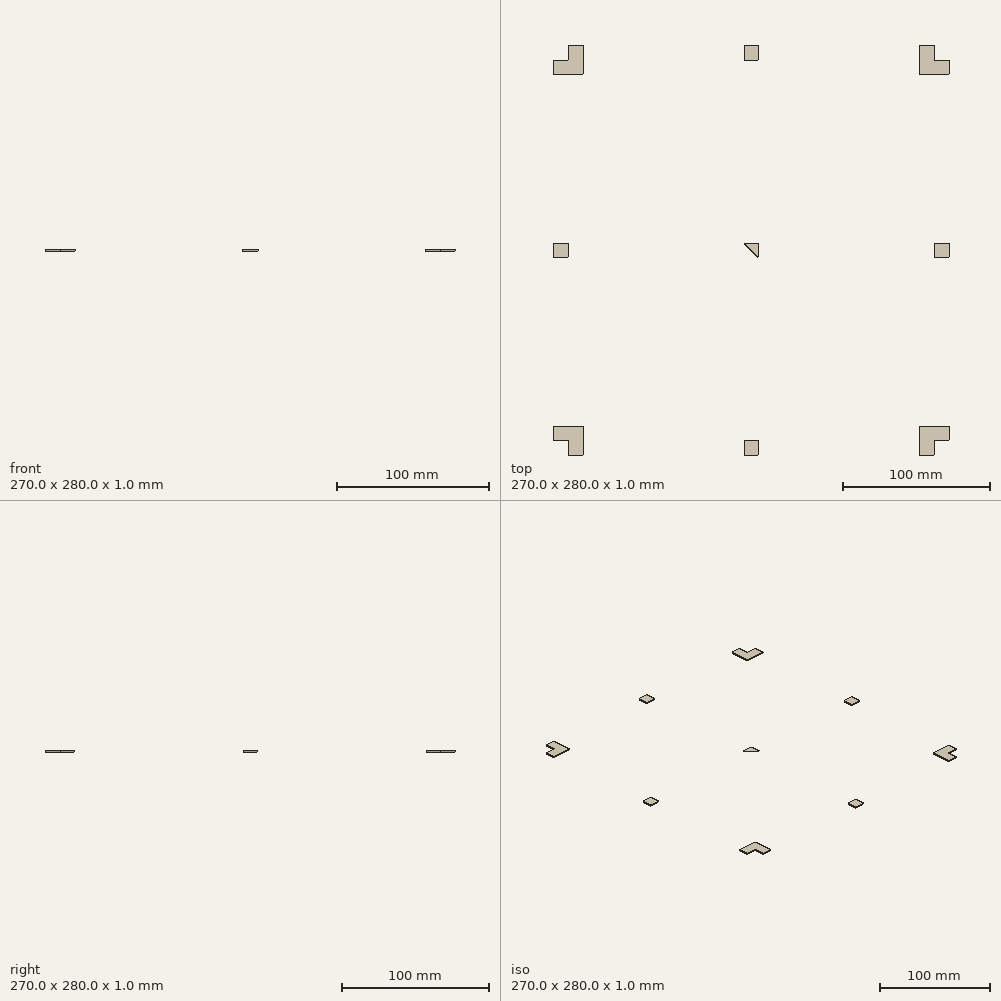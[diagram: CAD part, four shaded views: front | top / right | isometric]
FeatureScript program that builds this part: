
annotation { "Feature Type Name" : "Feature", "Feature Type Description" : "" }
export const myFeature = defineFeature(function(context is Context, id is Id, definition is map)
    precondition{}
    {
        {
            var Q0;
            Q0=qCreatedBy(makeId("Top.planeOp"),FACE);
            var sketch = newSketch(context, id + "F0", { "sketchPlane" : qUnion([Q0])});
            skLineSegment(sketch, "E0.bottom", {"start": v(-135, 140) * mm, "end": v(-115, 140) * mm});
            skLineSegment(sketch, "E0.top", {"start": v(-135, 120) * mm, "end": v(-115, 120) * mm});
            skLineSegment(sketch, "E0.left", {"start": v(-135, 140) * mm, "end": v(-135, 120) * mm});
            skLineSegment(sketch, "E0.right", {"start": v(-115, 140) * mm, "end": v(-115, 120) * mm});
            skSolve(sketch);
        }
        {
            var Q0;
            Q0 = qSketchRegion(id + "F0", true);
            extrude(context, id + "F1", {"entities" : qUnion([Q0]), "oppositeDirection" : true, "depth" : 1 * mm});
        }
        {
            var Q0;
            Q0=makeQuery(id+"F1.opExtrude","CAP_FACE",FACE,{"disambiguationData":[OSD([sQuery(id+"F0.wireOp",EDGE,"E0.bottom"),sQuery(id+"F0.wireOp",EDGE,"E0.top"),sQuery(id+"F0.wireOp",EDGE,"E0.left"),sQuery(id+"F0.wireOp",EDGE,"E0.right")])],"isStart":false});
            var sketch = newSketch(context, id + "F2", { "sketchPlane" : qUnion([Q0])});
            skPoint(sketch, "E1.oppositeSnap0", {"position": v(-115, -130) * mm});
            skLineSegment(sketch, "E1.bottom", {"start": v(-135, -140) * mm, "end": v(-125, -140) * mm});
            skLineSegment(sketch, "E1.top", {"start": v(-135, -130) * mm, "end": v(-125, -130) * mm});
            skLineSegment(sketch, "E1.left", {"start": v(-135, -130) * mm, "end": v(-135, -140) * mm});
            skLineSegment(sketch, "E1.right", {"start": v(-125, -130) * mm, "end": v(-125, -140) * mm});
            skSolve(sketch);
        }
        {
            var Q0;
            Q0=qCreatedBy(makeId("Top.planeOp"),FACE);
            var sketch = newSketch(context, id + "F3", { "sketchPlane" : qUnion([Q0])});
            skLineSegment(sketch, "E2.bottom", {"start": v(-135, 5) * mm, "end": v(-125, 5) * mm});
            skLineSegment(sketch, "E2.top", {"start": v(-135, -5) * mm, "end": v(-125, -5) * mm});
            skLineSegment(sketch, "E2.left", {"start": v(-135, 5) * mm, "end": v(-135, -5) * mm});
            skLineSegment(sketch, "E2.right", {"start": v(-125, 5) * mm, "end": v(-125, -5) * mm});
            skSolve(sketch);
        }
        {
            var Q0;
            Q0 = qSketchRegion(id + "F2", true);
            extrude(context, id + "F4", {"entities" : qUnion([Q0]), "operationType" : NewBodyOperationType.REMOVE, "oppositeDirection" : true, "depth" : 1 * mm});
        }
        {
            var Q0;
            Q0=makeQuery(id+"F1.opExtrude","SWEPT_BODY",BODY,{"disambiguationData":[OSD([sQuery(id+"F0.wireOp",EDGE,"E0.bottom"),sQuery(id+"F0.wireOp",EDGE,"E0.top"),sQuery(id+"F0.wireOp",EDGE,"E0.left"),sQuery(id+"F0.wireOp",EDGE,"E0.right")])]});
            var Q1;
            Q1=qCreatedBy(makeId("Right.planeOp"),FACE);
            mirror(context, id + "F5", {"entities" : qUnion([Q0]), "mirrorPlane" : qUnion([Q1])});
        }
        {
            var Q0;
            Q0=makeQuery(id+"F1.opExtrude","SWEPT_BODY",BODY,{"disambiguationData":[OSD([sQuery(id+"F0.wireOp",EDGE,"E0.bottom"),sQuery(id+"F0.wireOp",EDGE,"E0.top"),sQuery(id+"F0.wireOp",EDGE,"E0.left"),sQuery(id+"F0.wireOp",EDGE,"E0.right")])]});
            var Q1;
            Q1=qCreatedBy(makeId("Front.planeOp"),FACE);
            mirror(context, id + "F6", {"operationType" : NewBodyOperationType.ADD, "entities" : qUnion([Q0]), "mirrorPlane" : qUnion([Q1])});
        }
        {
            var Q0;
            Q0=makeQuery(id+"F5.opPattern","COPY",BODY,{"derivedFrom":makeQuery(id+"F1.opExtrude","SWEPT_BODY",BODY,{"disambiguationData":[OSD([sQuery(id+"F0.wireOp",EDGE,"E0.bottom"),sQuery(id+"F0.wireOp",EDGE,"E0.top"),sQuery(id+"F0.wireOp",EDGE,"E0.left"),sQuery(id+"F0.wireOp",EDGE,"E0.right")])]}),"instanceName":"1"});
            var Q1;
            Q1=qCreatedBy(makeId("Front.planeOp"),FACE);
            mirror(context, id + "F7", {"entities" : qUnion([Q0]), "mirrorPlane" : qUnion([Q1])});
        }
        {
            var Q0;
            Q0=makeQuery(id+"F3.imprint","IMPRINT",FACE,{"disambiguationData":[TD([[makeQuery(id+"F3.imprint","IMPRINT",EDGE,{"derivedFrom":sQuery(id+"F3.wireOp",EDGE,"E2.bottom")}),-1.0]])]});
            extrude(context, id + "F8", {"entities" : qUnion([Q0]), "depth" : 1 * mm});
        }
        {
            var Q0;
            Q0=makeQuery(id+"F8.opExtrude","SWEPT_BODY",BODY,{"disambiguationData":[OSD([sQuery(id+"F3.wireOp",EDGE,"E2.bottom"),sQuery(id+"F3.wireOp",EDGE,"E2.top"),sQuery(id+"F3.wireOp",EDGE,"E2.left"),sQuery(id+"F3.wireOp",EDGE,"E2.right")])]});
            var Q1;
            Q1=qCreatedBy(makeId("Right.planeOp"),FACE);
            mirror(context, id + "F9", {"entities" : qUnion([Q0]), "mirrorPlane" : qUnion([Q1])});
        }
        {
            var Q0;
            Q0=qCreatedBy(makeId("Top.planeOp"),FACE);
            var sketch = newSketch(context, id + "F10", { "sketchPlane" : qUnion([Q0])});
            skLineSegment(sketch, "E3.bottom", {"start": v(-5, 140) * mm, "end": v(5, 140) * mm});
            skLineSegment(sketch, "E3.top", {"start": v(-5, 130) * mm, "end": v(5, 130) * mm});
            skLineSegment(sketch, "E3.left", {"start": v(-5, 140) * mm, "end": v(-5, 130) * mm});
            skLineSegment(sketch, "E3.right", {"start": v(5, 140) * mm, "end": v(5, 130) * mm});
            skSolve(sketch);
        }
        {
            var Q0;
            Q0=makeQuery(id+"F10.imprint","IMPRINT",FACE,{"disambiguationData":[TD([[makeQuery(id+"F10.imprint","IMPRINT",EDGE,{"derivedFrom":sQuery(id+"F10.wireOp",EDGE,"E3.bottom")}),-1.0]])]});
            extrude(context, id + "F11", {"entities" : qUnion([Q0]), "depth" : 1 * mm});
        }
        {
            var Q0;
            Q0=makeQuery(id+"F11.opExtrude","SWEPT_BODY",BODY,{"disambiguationData":[OSD([sQuery(id+"F10.wireOp",EDGE,"E3.bottom"),sQuery(id+"F10.wireOp",EDGE,"E3.top"),sQuery(id+"F10.wireOp",EDGE,"E3.left"),sQuery(id+"F10.wireOp",EDGE,"E3.right")])]});
            var Q1;
            Q1=qCreatedBy(makeId("Front.planeOp"),FACE);
            mirror(context, id + "F12", {"entities" : qUnion([Q0]), "mirrorPlane" : qUnion([Q1])});
        }
        {
            var Q0;
            Q0=qCreatedBy(makeId("Top.planeOp"),FACE);
            var sketch = newSketch(context, id + "F13", { "sketchPlane" : qUnion([Q0])});
            skLineSegment(sketch, "E4", {"start": v(-5, 5) * mm, "end": v(5, 5) * mm});
            skLineSegment(sketch, "E5", {"start": v(5, 5) * mm, "end": v(5, -5) * mm});
            skLineSegment(sketch, "E6", {"start": v(5, -5) * mm, "end": v(-5, 5) * mm});
            skSolve(sketch);
        }
        {
            var Q0;
            Q0=makeQuery(id+"F13.imprint","IMPRINT",FACE,{"disambiguationData":[TD([[makeQuery(id+"F13.imprint","IMPRINT",EDGE,{"derivedFrom":sQuery(id+"F13.wireOp",EDGE,"E4")}),-1.0]])]});
            extrude(context, id + "F14", {"entities" : qUnion([Q0]), "depth" : 1 * mm});
        }
        {
            var Q0;
            Q0=makeQuery(id+"F8.opExtrude","SWEPT_BODY",BODY,{"disambiguationData":[OSD([sQuery(id+"F3.wireOp",EDGE,"E2.bottom"),sQuery(id+"F3.wireOp",EDGE,"E2.top"),sQuery(id+"F3.wireOp",EDGE,"E2.left"),sQuery(id+"F3.wireOp",EDGE,"E2.right")])]});
            transform(context, id + "F15", {"entities" : qUnion([Q0]), "transformType" : TransformType.TRANSLATION_3D, "dx" : 0 * mm, "dy" : 0 * mm, "dz" : -2 * mm, "makeCopy" : false});
        }
        {
            var Q0;
            Q0=makeQuery(id+"F12.opPattern","COPY",BODY,{"derivedFrom":makeQuery(id+"F11.opExtrude","SWEPT_BODY",BODY,{"disambiguationData":[OSD([sQuery(id+"F10.wireOp",EDGE,"E3.bottom"),sQuery(id+"F10.wireOp",EDGE,"E3.top"),sQuery(id+"F10.wireOp",EDGE,"E3.left"),sQuery(id+"F10.wireOp",EDGE,"E3.right")])]}),"instanceName":"1"});
            transform(context, id + "F16", {"entities" : qUnion([Q0]), "transformType" : TransformType.TRANSLATION_3D, "dx" : 0 * mm, "dy" : 0 * mm, "dz" : -2 * mm, "makeCopy" : false});
        }
        {
            var Q0;
            Q0=makeQuery(id+"F14.opExtrude","SWEPT_BODY",BODY,{"disambiguationData":[OSD([sQuery(id+"F13.wireOp",EDGE,"E4"),sQuery(id+"F13.wireOp",EDGE,"E5"),sQuery(id+"F13.wireOp",EDGE,"E6")])]});
            transform(context, id + "F17", {"entities" : qUnion([Q0]), "transformType" : TransformType.TRANSLATION_3D, "dx" : 0 * mm, "dy" : 0 * mm, "dz" : -2 * mm, "makeCopy" : false});
        }
        {
            var Q0;
            Q0=makeQuery(id+"F11.opExtrude","SWEPT_BODY",BODY,{"disambiguationData":[OSD([sQuery(id+"F10.wireOp",EDGE,"E3.bottom"),sQuery(id+"F10.wireOp",EDGE,"E3.top"),sQuery(id+"F10.wireOp",EDGE,"E3.left"),sQuery(id+"F10.wireOp",EDGE,"E3.right")])]});
            transform(context, id + "F18", {"entities" : qUnion([Q0]), "transformType" : TransformType.TRANSLATION_3D, "dx" : 0 * mm, "dy" : 0 * mm, "dz" : -2 * mm, "makeCopy" : false});
        }
        {
            var Q0;
            Q0=makeQuery(id+"F9.opPattern","COPY",BODY,{"derivedFrom":makeQuery(id+"F8.opExtrude","SWEPT_BODY",BODY,{"disambiguationData":[OSD([sQuery(id+"F3.wireOp",EDGE,"E2.bottom"),sQuery(id+"F3.wireOp",EDGE,"E2.top"),sQuery(id+"F3.wireOp",EDGE,"E2.left"),sQuery(id+"F3.wireOp",EDGE,"E2.right")])]}),"instanceName":"1"});
            transform(context, id + "F19", {"entities" : qUnion([Q0]), "transformType" : TransformType.TRANSLATION_3D, "dx" : 0 * mm, "dy" : 0 * mm, "dz" : -2 * mm, "makeCopy" : false});
        }
        {
            var Q0;
            Q0=makeQuery(id+"F12.opPattern","COPY",BODY,{"derivedFrom":makeQuery(id+"F11.opExtrude","SWEPT_BODY",BODY,{"disambiguationData":[OSD([sQuery(id+"F10.wireOp",EDGE,"E3.bottom"),sQuery(id+"F10.wireOp",EDGE,"E3.top"),sQuery(id+"F10.wireOp",EDGE,"E3.left"),sQuery(id+"F10.wireOp",EDGE,"E3.right")])]}),"instanceName":"1"});
            var Q1;
            Q1=makeQuery(id+"F14.opExtrude","SWEPT_BODY",BODY,{"disambiguationData":[OSD([sQuery(id+"F13.wireOp",EDGE,"E4"),sQuery(id+"F13.wireOp",EDGE,"E5"),sQuery(id+"F13.wireOp",EDGE,"E6")])]});
            var Q2;
            Q2=makeQuery(id+"F11.opExtrude","SWEPT_BODY",BODY,{"disambiguationData":[OSD([sQuery(id+"F10.wireOp",EDGE,"E3.bottom"),sQuery(id+"F10.wireOp",EDGE,"E3.top"),sQuery(id+"F10.wireOp",EDGE,"E3.left"),sQuery(id+"F10.wireOp",EDGE,"E3.right")])]});
            transform(context, id + "F20", {"entities" : qUnion([Q0, Q1, Q2]), "transformType" : TransformType.TRANSLATION_3D, "dx" : 0 * mm, "dy" : 0 * mm, "dz" : 1 * mm, "makeCopy" : false});
        }
        {
            var Q0;
            Q0=makeQuery(id+"F6.opPattern","COPY",BODY,{"derivedFrom":makeQuery(id+"F1.opExtrude","SWEPT_BODY",BODY,{"disambiguationData":[OSD([sQuery(id+"F0.wireOp",EDGE,"E0.bottom"),sQuery(id+"F0.wireOp",EDGE,"E0.top"),sQuery(id+"F0.wireOp",EDGE,"E0.left"),sQuery(id+"F0.wireOp",EDGE,"E0.right")])]}),"instanceName":"1"});
            var Q1;
            Q1=makeQuery(id+"F8.opExtrude","SWEPT_BODY",BODY,{"disambiguationData":[OSD([sQuery(id+"F3.wireOp",EDGE,"E2.bottom"),sQuery(id+"F3.wireOp",EDGE,"E2.top"),sQuery(id+"F3.wireOp",EDGE,"E2.left"),sQuery(id+"F3.wireOp",EDGE,"E2.right")])]});
            transform(context, id + "F21", {"entities" : qUnion([Q0, Q1]), "transformType" : TransformType.TRANSLATION_3D, "dx" : 0 * mm, "dy" : 0 * mm, "dz" : 1 * mm, "makeCopy" : false});
        }
        {
            var Q0;
            Q0=makeQuery(id+"F1.opExtrude","SWEPT_BODY",BODY,{"disambiguationData":[OSD([sQuery(id+"F0.wireOp",EDGE,"E0.bottom"),sQuery(id+"F0.wireOp",EDGE,"E0.top"),sQuery(id+"F0.wireOp",EDGE,"E0.left"),sQuery(id+"F0.wireOp",EDGE,"E0.right")])]});
            transform(context, id + "F22", {"entities" : qUnion([Q0]), "transformType" : TransformType.TRANSLATION_3D, "dx" : 0 * mm, "dy" : 0 * mm, "dz" : 1 * mm, "makeCopy" : false});
        }
        {
            var Q0;
            Q0=makeQuery(id+"F8.opExtrude","SWEPT_BODY",BODY,{"disambiguationData":[OSD([sQuery(id+"F3.wireOp",EDGE,"E2.bottom"),sQuery(id+"F3.wireOp",EDGE,"E2.top"),sQuery(id+"F3.wireOp",EDGE,"E2.left"),sQuery(id+"F3.wireOp",EDGE,"E2.right")])]});
            transform(context, id + "F23", {"entities" : qUnion([Q0]), "transformType" : TransformType.TRANSLATION_3D, "dx" : 0 * mm, "dy" : 0 * mm, "dz" : 1 * mm, "makeCopy" : false});
        }
        {
            var Q0;
            Q0=makeQuery(id+"F12.opPattern","COPY",BODY,{"derivedFrom":makeQuery(id+"F11.opExtrude","SWEPT_BODY",BODY,{"disambiguationData":[OSD([sQuery(id+"F10.wireOp",EDGE,"E3.bottom"),sQuery(id+"F10.wireOp",EDGE,"E3.top"),sQuery(id+"F10.wireOp",EDGE,"E3.left"),sQuery(id+"F10.wireOp",EDGE,"E3.right")])]}),"instanceName":"1"});
            var Q1;
            Q1=makeQuery(id+"F14.opExtrude","SWEPT_BODY",BODY,{"disambiguationData":[OSD([sQuery(id+"F13.wireOp",EDGE,"E4"),sQuery(id+"F13.wireOp",EDGE,"E5"),sQuery(id+"F13.wireOp",EDGE,"E6")])]});
            var Q2;
            Q2=makeQuery(id+"F11.opExtrude","SWEPT_BODY",BODY,{"disambiguationData":[OSD([sQuery(id+"F10.wireOp",EDGE,"E3.bottom"),sQuery(id+"F10.wireOp",EDGE,"E3.top"),sQuery(id+"F10.wireOp",EDGE,"E3.left"),sQuery(id+"F10.wireOp",EDGE,"E3.right")])]});
            transform(context, id + "F24", {"entities" : qUnion([Q0, Q1, Q2]), "transformType" : TransformType.TRANSLATION_3D, "dx" : 0 * mm, "dy" : 0 * mm, "dz" : 1 * mm, "makeCopy" : false});
        }
        {
            var Q0;
            Q0=makeQuery(id+"F9.opPattern","COPY",BODY,{"derivedFrom":makeQuery(id+"F8.opExtrude","SWEPT_BODY",BODY,{"disambiguationData":[OSD([sQuery(id+"F3.wireOp",EDGE,"E2.bottom"),sQuery(id+"F3.wireOp",EDGE,"E2.top"),sQuery(id+"F3.wireOp",EDGE,"E2.left"),sQuery(id+"F3.wireOp",EDGE,"E2.right")])]}),"instanceName":"1"});
            transform(context, id + "F25", {"entities" : qUnion([Q0]), "transformType" : TransformType.TRANSLATION_3D, "dx" : 0 * mm, "dy" : 0 * mm, "dz" : 1 * mm, "makeCopy" : false});
        }
        {
            var Q0;
            Q0=makeQuery(id+"F14.opExtrude","SWEPT_BODY",BODY,{"disambiguationData":[OSD([sQuery(id+"F13.wireOp",EDGE,"E4"),sQuery(id+"F13.wireOp",EDGE,"E5"),sQuery(id+"F13.wireOp",EDGE,"E6")])]});
            transform(context, id + "F26", {"entities" : qUnion([Q0]), "transformType" : TransformType.TRANSLATION_3D, "dx" : 0 * mm, "dy" : 0 * mm, "dz" : -1 * mm, "makeCopy" : false});
        }
        {
            var Q0;
            Q0=makeQuery(id+"F8.opExtrude","SWEPT_BODY",BODY,{"disambiguationData":[OSD([sQuery(id+"F3.wireOp",EDGE,"E2.bottom"),sQuery(id+"F3.wireOp",EDGE,"E2.top"),sQuery(id+"F3.wireOp",EDGE,"E2.left"),sQuery(id+"F3.wireOp",EDGE,"E2.right")])]});
            transform(context, id + "F27", {"entities" : qUnion([Q0]), "transformType" : TransformType.TRANSLATION_3D, "dx" : 0 * mm, "dy" : 0 * mm, "dz" : -1 * mm, "makeCopy" : false});
        }
        {
            var Q0;
            Q0=makeQuery(id+"F6.opPattern","COPY",BODY,{"derivedFrom":makeQuery(id+"F1.opExtrude","SWEPT_BODY",BODY,{"disambiguationData":[OSD([sQuery(id+"F0.wireOp",EDGE,"E0.bottom"),sQuery(id+"F0.wireOp",EDGE,"E0.top"),sQuery(id+"F0.wireOp",EDGE,"E0.left"),sQuery(id+"F0.wireOp",EDGE,"E0.right")])]}),"instanceName":"1"});
            transform(context, id + "F28", {"entities" : qUnion([Q0]), "transformType" : TransformType.TRANSLATION_3D, "dx" : 0 * mm, "dy" : 0 * mm, "dz" : -1 * mm, "makeCopy" : false});
        }
        {
            var Q0;
            Q0=makeQuery(id+"F12.opPattern","COPY",BODY,{"derivedFrom":makeQuery(id+"F11.opExtrude","SWEPT_BODY",BODY,{"disambiguationData":[OSD([sQuery(id+"F10.wireOp",EDGE,"E3.bottom"),sQuery(id+"F10.wireOp",EDGE,"E3.top"),sQuery(id+"F10.wireOp",EDGE,"E3.left"),sQuery(id+"F10.wireOp",EDGE,"E3.right")])]}),"instanceName":"1"});
            transform(context, id + "F29", {"entities" : qUnion([Q0]), "transformType" : TransformType.TRANSLATION_3D, "dx" : 0 * mm, "dy" : 0 * mm, "dz" : -1 * mm, "makeCopy" : false});
        }
        {
            var Q0;
            Q0=makeQuery(id+"F11.opExtrude","SWEPT_BODY",BODY,{"disambiguationData":[OSD([sQuery(id+"F10.wireOp",EDGE,"E3.bottom"),sQuery(id+"F10.wireOp",EDGE,"E3.top"),sQuery(id+"F10.wireOp",EDGE,"E3.left"),sQuery(id+"F10.wireOp",EDGE,"E3.right")])]});
            transform(context, id + "F30", {"entities" : qUnion([Q0]), "transformType" : TransformType.TRANSLATION_3D, "dx" : 0 * mm, "dy" : 0 * mm, "dz" : -1 * mm, "makeCopy" : false});
        }
        {
            var Q0;
            Q0=makeQuery(id+"F1.opExtrude","SWEPT_BODY",BODY,{"disambiguationData":[OSD([sQuery(id+"F0.wireOp",EDGE,"E0.bottom"),sQuery(id+"F0.wireOp",EDGE,"E0.top"),sQuery(id+"F0.wireOp",EDGE,"E0.left"),sQuery(id+"F0.wireOp",EDGE,"E0.right")])]});
            transform(context, id + "F31", {"entities" : qUnion([Q0]), "transformType" : TransformType.TRANSLATION_3D, "dx" : 0 * mm, "dy" : 0 * mm, "dz" : -1 * mm, "makeCopy" : false});
        }
    });
